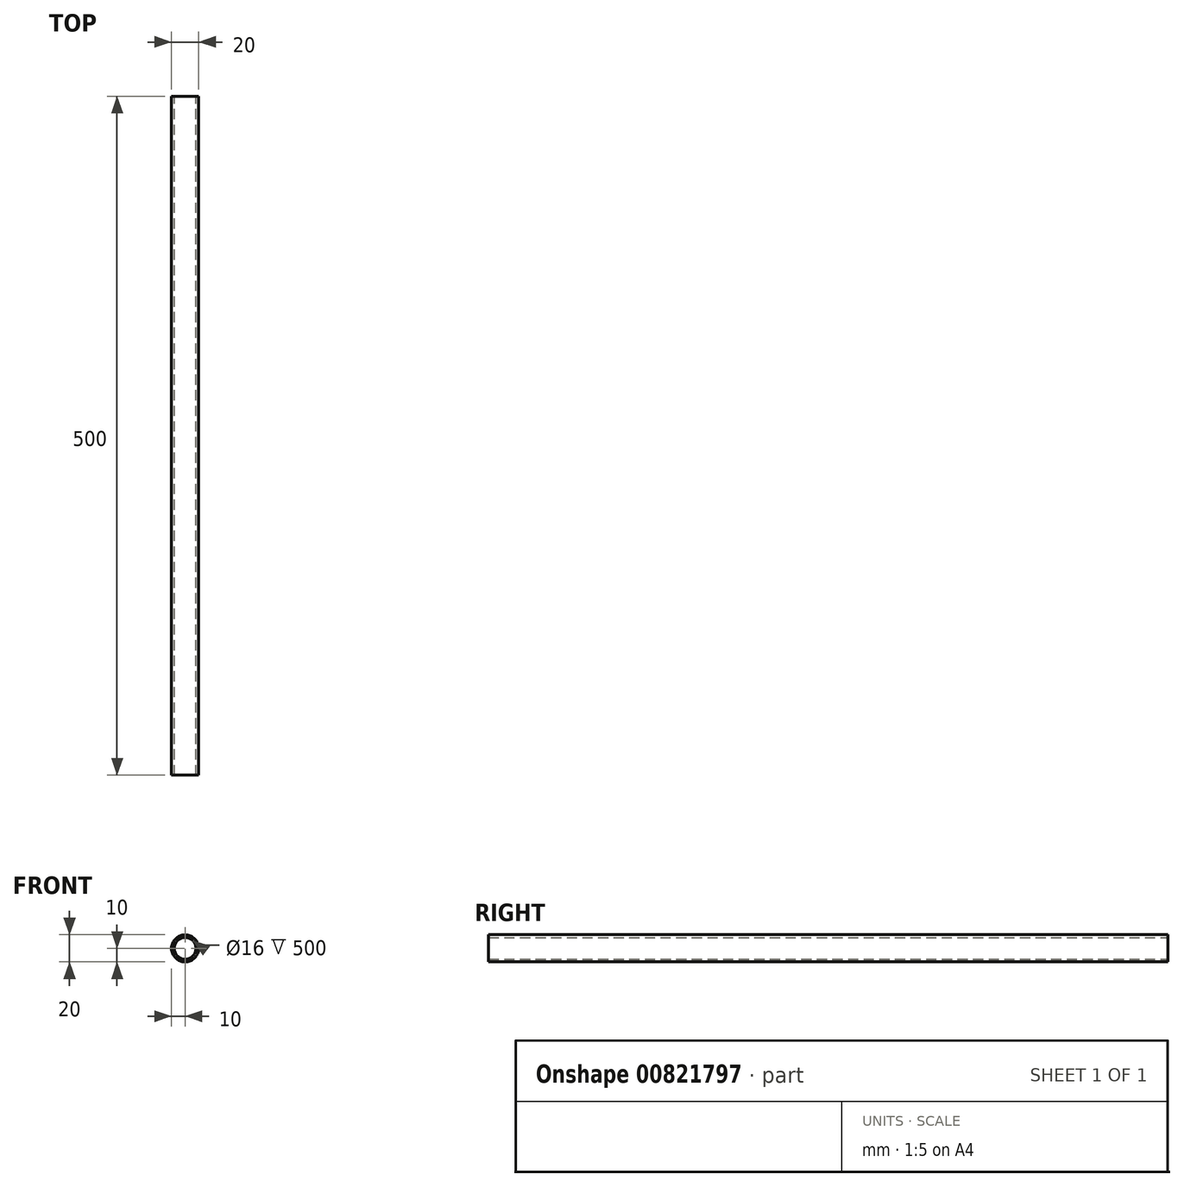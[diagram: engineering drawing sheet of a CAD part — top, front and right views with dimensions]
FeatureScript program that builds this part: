
annotation { "Feature Type Name" : "Feature", "Feature Type Description" : "" }
export const myFeature = defineFeature(function(context is Context, id is Id, definition is map)
    precondition{}
    {
        {
            var Q0;
            Q0=qCreatedBy(makeId("Front.planeOp"),FACE);
            var sketch = newSketch(context, id + "F0", { "sketchPlane" : qUnion([Q0])});
            skCircle(sketch, "E0", {"center": v(0, 0) * mm, "radius": 10 * mm});
            skCircle(sketch, "E1", {"center": v(0, 0) * mm, "radius": 8 * mm});
            skSolve(sketch);
        }
        {
            assignVariable(context, id + "F1", {"name" : "alu_rod_length", "anyValue" : 500});
        }
        {
            var Q0;
            Q0=makeQuery(id+"F0.imprint","IMPRINT",FACE,{"disambiguationData":[TD([[makeQuery(id+"F0.imprint","IMPRINT",EDGE,{"derivedFrom":sQuery(id+"F0.wireOp",EDGE,"E0")}),1.0]])]});
            extrude(context, id + "F2", {"entities" : qUnion([Q0]), "depth" : (getVariable(context, 'alu_rod_length')) * mm, "offsetDistance" : 25 * mm});
        }
        {
            var Q0;
            Q0=qCreatedBy(makeId("Front.planeOp"),FACE);
            var sketch = newSketch(context, id + "F3", { "sketchPlane" : qUnion([Q0])});
            skLineSegment(sketch, "E2", {"start": v(0, 38.77) * mm, "end": v(0, 0) * mm, "construction": true});
            skLineSegment(sketch, "E3", {"start": v(0, 0) * mm, "end": v(-36.77, 0) * mm, "construction": true});
            skSolve(sketch);
        }
    });
